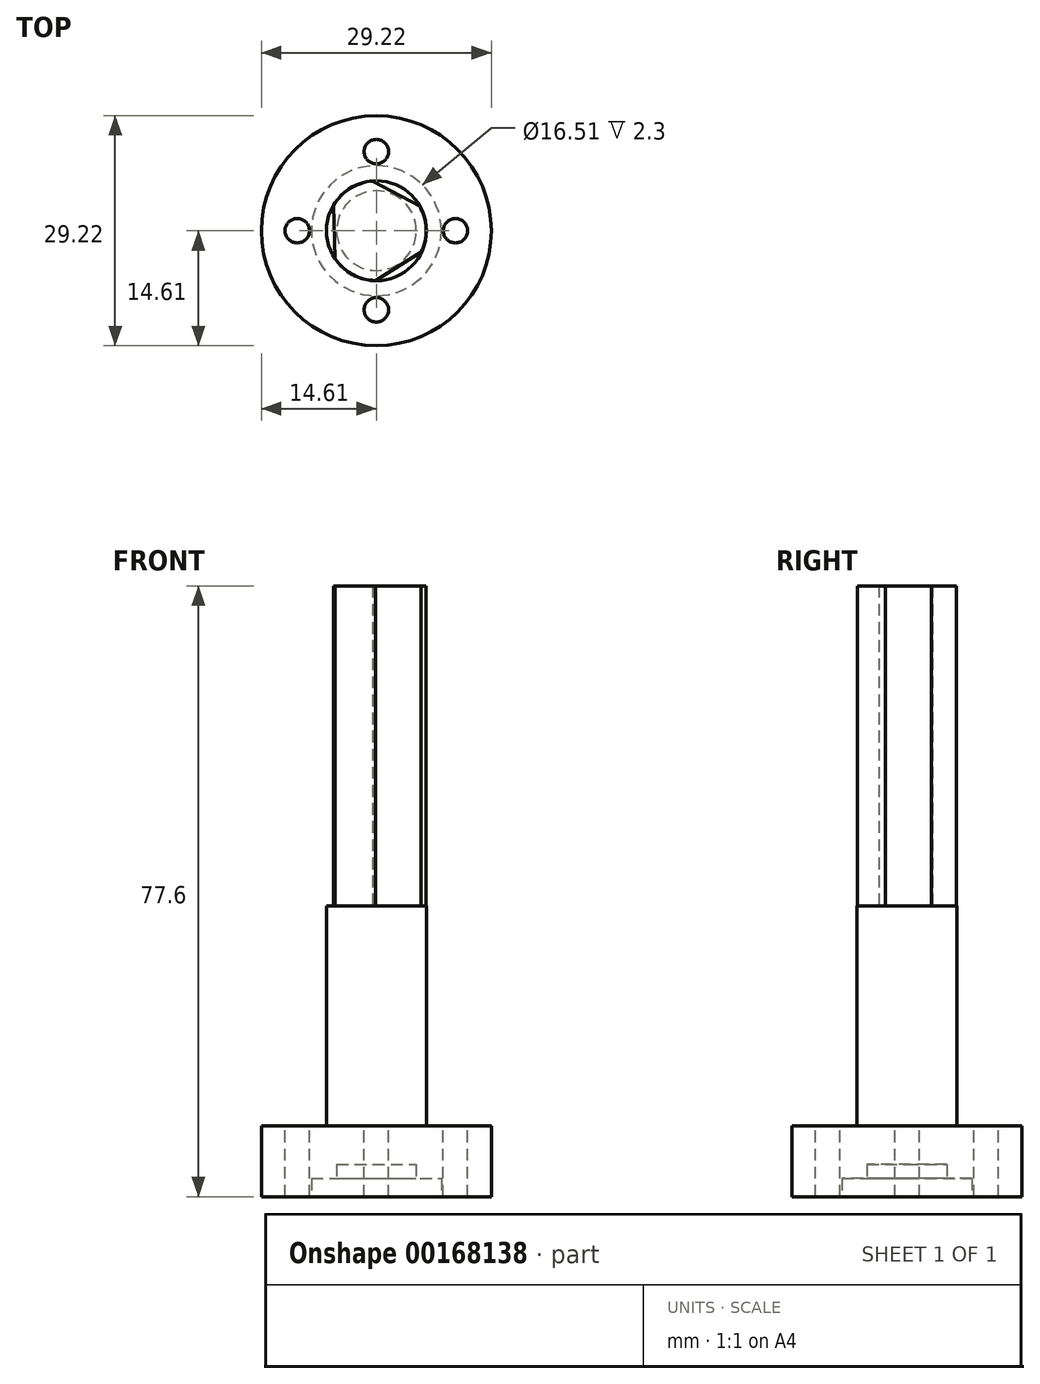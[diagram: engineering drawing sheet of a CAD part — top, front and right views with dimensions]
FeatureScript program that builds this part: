
annotation { "Feature Type Name" : "Feature", "Feature Type Description" : "" }
export const myFeature = defineFeature(function(context is Context, id is Id, definition is map)
    precondition{}
    {
        {
            var Q0;
            Q0=qCreatedBy(makeId("Top.planeOp"),FACE);
            var sketch = newSketch(context, id + "F0", { "sketchPlane" : qUnion([Q0])});
            skCircle(sketch, "E0", {"center": v(0, 0) * mm, "radius": 14.6 * mm});
            skSolve(sketch);
        }
        {
            var Q0;
            Q0=makeQuery(id+"F0.imprint","IMPRINT",FACE,{"disambiguationData":[TD([[makeQuery(id+"F0.imprint","IMPRINT",EDGE,{"derivedFrom":sQuery(id+"F0.wireOp",EDGE,"E0")}),1.0]])]});
            extrude(context, id + "F1", {"entities" : qUnion([Q0]), "depth" : 9.02 * mm});
        }
        {
            var Q0;
            Q0=makeQuery(id+"F1.opExtrude","CAP_FACE",FACE,{"disambiguationData":[OSD([sQuery(id+"F0.wireOp",EDGE,"E0")])],"isStart":false});
            var sketch = newSketch(context, id + "F2", { "sketchPlane" : qUnion([Q0])});
            skCircle(sketch, "E1", {"center": v(0, 0) * mm, "radius": 6.35 * mm});
            skSolve(sketch);
        }
        {
            var Q0;
            Q0=qSketchRegion(id+"F2",true);
            extrude(context, id + "F3", {"entities" : qUnion([Q0]), "operationType" : NewBodyOperationType.ADD, "depth" : 27.94 * mm});
        }
        {
            var Q0;
            Q0=makeQuery(id+"F3.opExtrude","CAP_FACE",FACE,{"disambiguationData":[OSD([sQuery(id+"F2.wireOp",EDGE,"E1")])],"isStart":false});
            var sketch = newSketch(context, id + "F4", { "sketchPlane" : qUnion([Q0])});
            skCircle(sketch, "E2.cCircle", {"center": v(0, 0) * mm, "radius": 5.33 * mm, "construction": true});
            skLineSegment(sketch, "E2.0", {"start": v(10.66, 0.33) * mm, "end": v(-5.04, -9.4) * mm});
            skLineSegment(sketch, "E2.1", {"start": v(-5.04, -9.4) * mm, "end": v(-5.62, 9.07) * mm});
            skLineSegment(sketch, "E2.2", {"start": v(-5.62, 9.07) * mm, "end": v(10.66, 0.33) * mm});
            skPoint(sketch, "E2.0.midPoint", {"position": v(2.8, -4.53) * mm});
            skSolve(sketch);
        }
        {
            var Q0;
            Q0=qSketchRegion(id+"F4",true);
            extrude(context, id + "F5", {"entities" : qUnion([Q0]), "operationType" : NewBodyOperationType.ADD, "depth" : 40.64 * mm});
        }
        {
            var Q0;
            Q0=makeQuery(id+"F1.opExtrude","CAP_FACE",FACE,{"disambiguationData":[OSD([sQuery(id+"F0.wireOp",EDGE,"E0")])],"isStart":true});
            var sketch = newSketch(context, id + "F6", { "sketchPlane" : qUnion([Q0])});
            skCircle(sketch, "E3", {"center": v(0, 0) * mm, "radius": 8.26 * mm});
            skSolve(sketch);
        }
        {
            var Q0;
            Q0=qSketchRegion(id+"F6",true);
            extrude(context, id + "F7", {"entities" : qUnion([Q0]), "operationType" : NewBodyOperationType.REMOVE, "oppositeDirection" : true, "depth" : 2.3 * mm});
        }
        {
            var Q0;
            Q0=makeQuery(id+"F1.opExtrude","CAP_FACE",FACE,{"disambiguationData":[OSD([sQuery(id+"F0.wireOp",EDGE,"E0")])],"isStart":true});
            var sketch = newSketch(context, id + "F8", { "sketchPlane" : qUnion([Q0])});
            skCircle(sketch, "E4", {"center": v(0, 0) * mm, "radius": 5.06 * mm});
            skSolve(sketch);
        }
        {
            var Q0;
            Q0=qSketchRegion(id+"F8",true);
            extrude(context, id + "F9", {"entities" : qUnion([Q0]), "operationType" : NewBodyOperationType.REMOVE, "oppositeDirection" : true, "depth" : 4.1 * mm});
        }
        {
            var Q0;
            Q0=makeQuery(id+"F1.opExtrude","CAP_FACE",FACE,{"disambiguationData":[OSD([sQuery(id+"F0.wireOp",EDGE,"E0")])],"isStart":false});
            var sketch = newSketch(context, id + "F10", { "sketchPlane" : qUnion([Q0])});
            skPoint(sketch, "E5", {"position": v(-10.05, 0) * mm});
            skPoint(sketch, "E6", {"position": v(0, 10.05) * mm});
            skPoint(sketch, "E7", {"position": v(10.05, 0) * mm});
            skPoint(sketch, "E8", {"position": v(0, -10.05) * mm});
            skCircle(sketch, "E9", {"center": v(0, 0) * mm, "radius": 10.05 * mm, "construction": true});
            skSolve(sketch);
        }
        {
            var Q0;
            Q0=sQuery(id+"F10.wireOp",VERTEX,"E8");
            var Q1;
            Q1=sQuery(id+"F10.wireOp",VERTEX,"E5");
            var Q2;
            Q2=sQuery(id+"F10.wireOp",VERTEX,"E6");
            var Q3;
            Q3=sQuery(id+"F10.wireOp",VERTEX,"E7");
            var Q4;
            Q4=makeQuery(id+"F1.opExtrude","SWEPT_BODY",BODY,{"disambiguationData":[OSD([sQuery(id+"F0.wireOp",EDGE,"E0")])]});
            hole(context, id + "F11", {"style" : HoleStyle.SIMPLE, "endStyle" : HoleEndStyle.THROUGH, "holeDiameter" : 3.1 * mm, "locations" : qUnion([Q0, Q1, Q2, Q3]), "scope" : qUnion([Q4]), "isTappedThrough" : true});
        }
        {
            var Q0;
            {var subQ0=sQuery(id+"F2.wireOp",EDGE,"E1");var subQ1=sQuery(id+"F4.wireOp",EDGE,"E2.0");Q0=makeQuery(id+"F5.boolean.opBoolean","SPLIT",FACE,{"disambiguationData":[TD([makeQuery(id+"F5.opExtrude","SWEPT_FACE",FACE,{"disambiguationData":[OSD([subQ1])]})])],"derivedFrom":makeQuery(id+"F3.opExtrude","CAP_FACE",FACE,{"disambiguationData":[OSD([subQ0])],"isStart":false})});}
            var sketch = newSketch(context, id + "F12", { "sketchPlane" : qUnion([Q0])});
            skCircle(sketch, "E10", {"center": v(0, 0) * mm, "radius": 6.32 * mm});
            skCircle(sketch, "E11", {"center": v(0, 0) * mm, "radius": 15.65 * mm});
            skSolve(sketch);
        }
        {
            var Q0;
            Q0=qSketchRegion(id+"F12",true);
            extrude(context, id + "F13", {"entities" : qUnion([Q0]), "operationType" : NewBodyOperationType.REMOVE, "endBound" : BoundingType.THROUGH_ALL, "depth" : 25.4 * mm});
        }
    });
